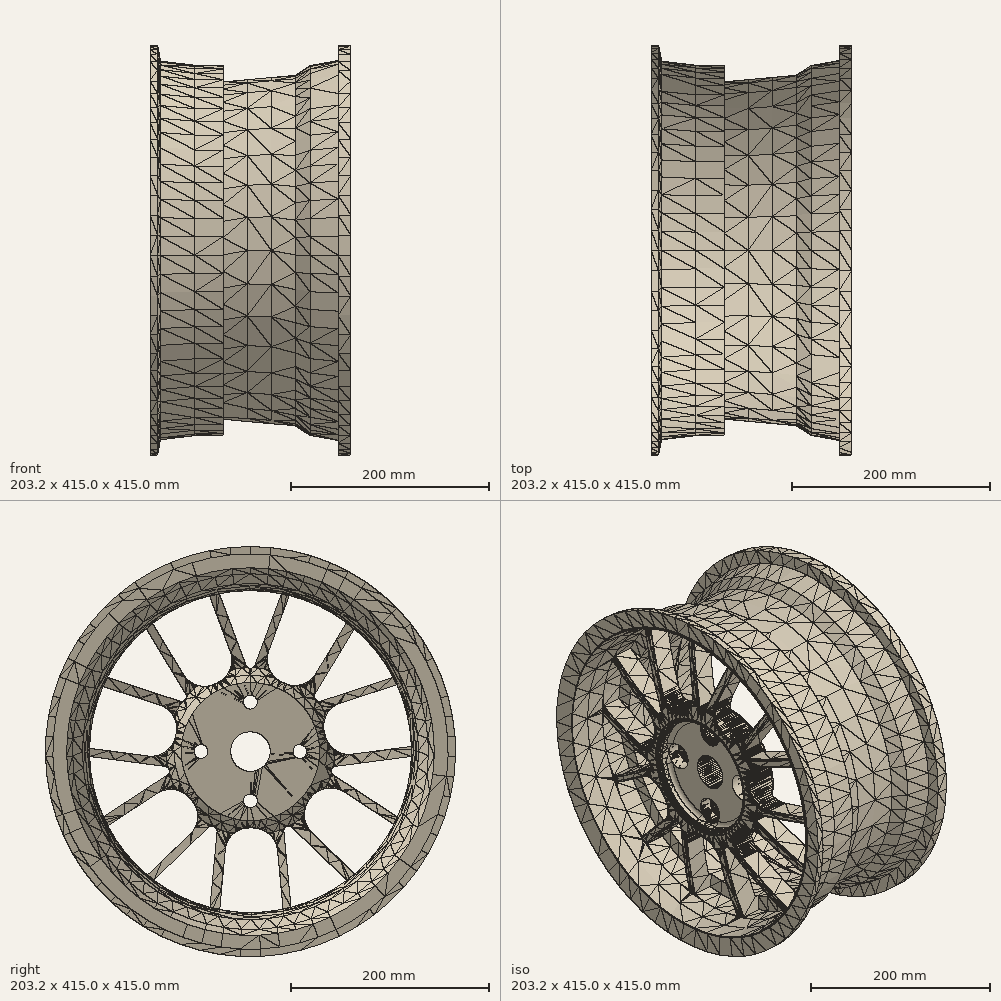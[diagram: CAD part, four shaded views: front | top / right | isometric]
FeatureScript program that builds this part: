
annotation { "Feature Type Name" : "Feature", "Feature Type Description" : "" }
export const myFeature = defineFeature(function(context is Context, id is Id, definition is map)
    precondition{}
    {
        {
            var Q0;
            Q0=qCreatedBy(makeId("Front.planeOp"),FACE);
            var sketch = newSketch(context, id + "F0", { "sketchPlane" : qUnion([Q0])});
            skLineSegment(sketch, "E0", {"start": v(0, 0) * mm, "end": v(203.2, 0) * mm});
            skLineSegment(sketch, "E1", {"start": v(203.2, 0) * mm, "end": v(203.2, 207.5) * mm});
            skPoint(sketch, "E2", {"position": v(203.2, 200) * mm});
            skLineSegment(sketch, "E3", {"start": v(203.2, 200) * mm, "end": v(197.7, 200) * mm});
            skPoint(sketch, "E4", {"position": v(197.7, 186) * mm});
            skLineSegment(sketch, "E5", {"start": v(197.7, 200) * mm, "end": v(197.7, 186) * mm});
            skPoint(sketch, "E6", {"position": v(164.7, 180) * mm});
            skLineSegment(sketch, "E7", {"start": v(164.7, 180) * mm, "end": v(197.7, 186) * mm});
            skPoint(sketch, "E8", {"position": v(149.7, 170) * mm});
            skLineSegment(sketch, "E9", {"start": v(164.7, 180) * mm, "end": v(149.7, 170) * mm});
            skPoint(sketch, "E10", {"position": v(66.7, 162.5) * mm});
            skLineSegment(sketch, "E11", {"start": v(66.7, 162.5) * mm, "end": v(149.7, 170) * mm});
            skLineSegment(sketch, "E12", {"start": v(203.2, 207.5) * mm, "end": v(66.7, 207.5) * mm});
            skLineSegment(sketch, "E13", {"start": v(0, 0) * mm, "end": v(0, 207.5) * mm});
            skPoint(sketch, "E14", {"position": v(2.5, 185) * mm});
            skPoint(sketch, "E15", {"position": v(45, 180) * mm});
            skLineSegment(sketch, "E16", {"start": v(45, 180) * mm, "end": v(66.7, 162.5) * mm});
            skLineSegment(sketch, "E17", {"start": v(2.5, 185) * mm, "end": v(45, 180) * mm});
            skLineSegment(sketch, "E18", {"start": v(0, 207.5) * mm, "end": v(66.7, 207.5) * mm});
            skLineSegment(sketch, "E19", {"start": v(2.5, 185) * mm, "end": v(0, 185) * mm});
            skLineSegment(sketch, "E20", {"start": v(2.5, 185) * mm, "end": v(2.5, 185.9) * mm});
            skLineSegment(sketch, "E21", {"start": v(3.1, 186.5) * mm, "end": v(3.4, 186.5) * mm});
            skLineSegment(sketch, "E22", {"start": v(0, 207.5) * mm, "end": v(4, 186.5) * mm});
            skPoint(sketch, "E23.visualSharp", {"position": v(2.5, 186.5) * mm});
            skArc(sketch, "E23.filletArc", {"start": v(3.1, 186.5) * mm, "mid": v(2.68, 186.32) * mm, "end": v(2.5, 185.9) * mm});
            skLineSegment(sketch, "E24", {"start": v(4, 185.9) * mm, "end": v(4, 185.5) * mm, "construction": true});
            skPoint(sketch, "E25.visualSharp", {"position": v(4, 186.5) * mm});
            skArc(sketch, "E25.filletArc", {"start": v(4, 185.9) * mm, "mid": v(3.82, 186.32) * mm, "end": v(3.4, 186.5) * mm});
            skLineSegment(sketch, "E26", {"start": v(4, 186.5) * mm, "end": v(4, 185.9) * mm});
            skLineSegment(sketch, "E27", {"start": v(66.7, 180) * mm, "end": v(45, 180) * mm});
            skLineSegment(sketch, "E28", {"start": v(66.7, 162.5) * mm, "end": v(66.7, 180) * mm});
            skArc(sketch, "E29", {"start": v(66.7, 162.5) * mm, "mid": v(58.94, 175.08) * mm, "end": v(45, 180) * mm});
            skLineSegment(sketch, "E30.0", {"start": v(203.2, 207.5) * mm, "end": v(190.2, 207.5) * mm});
            skLineSegment(sketch, "E30.1", {"start": v(66.03, 169.97) * mm, "end": v(66.7, 170.03) * mm});
            skLineSegment(sketch, "E30.2", {"start": v(161.83, 187.1) * mm, "end": v(147.13, 177.3) * mm});
            skLineSegment(sketch, "E30.3", {"start": v(161.83, 187.1) * mm, "end": v(190.2, 192.26) * mm});
            skLineSegment(sketch, "E30.4", {"start": v(190.2, 207.5) * mm, "end": v(190.2, 192.26) * mm});
            skLineSegment(sketch, "E31.0", {"start": v(10.67, 191.6) * mm, "end": v(45.44, 187.5) * mm});
            skLineSegment(sketch, "E31.1", {"start": v(7.63, 207.5) * mm, "end": v(10.67, 191.6) * mm});
            skLineSegment(sketch, "E32.0", {"start": v(74.2, 187.5) * mm, "end": v(45.44, 187.5) * mm});
            skLineSegment(sketch, "E32.1", {"start": v(74.2, 162.5) * mm, "end": v(74.2, 163.18) * mm});
            skLineSegment(sketch, "E33.trimOffspring", {"start": v(74.2, 170.7) * mm, "end": v(74.2, 187.5) * mm});
            skLineSegment(sketch, "E34.trimOffspring", {"start": v(74.2, 170.7) * mm, "end": v(147.13, 177.3) * mm});
            skPoint(sketch, "E35", {"position": v(45, -180) * mm});
            skPoint(sketch, "E36", {"position": v(16, 0) * mm});
            skArc(sketch, "E37", {"start": v(45, 180) * mm, "mid": v(23.3, 91.16) * mm, "end": v(16, 0) * mm});
            skArc(sketch, "E38.0", {"start": v(66.7, 162.54) * mm, "mid": v(48.21, 82.2) * mm, "end": v(42, 0) * mm});
            skLineSegment(sketch, "E39", {"start": v(16, 0) * mm, "end": v(42, 0) * mm});
            skLineSegment(sketch, "E40", {"start": v(16, 0) * mm, "end": v(16, 20) * mm});
            skLineSegment(sketch, "E41", {"start": v(16, 20) * mm, "end": v(76, 20) * mm});
            skPoint(sketch, "E42", {"position": v(66.2, 70) * mm});
            skPoint(sketch, "E43", {"position": v(48.64, 85) * mm});
            skLineSegment(sketch, "E44", {"start": v(66.2, 70) * mm, "end": v(48.64, 85) * mm});
            skLineSegment(sketch, "E45", {"start": v(66.2, 70) * mm, "end": v(66.2, 0) * mm});
            skSolve(sketch);
        }
        {
            var Q0;
            {var subQ3=sQuery(id+"F0.wireOp",EDGE,"E38.0");var subQ5=sQuery(id+"F0.wireOp",EDGE,"E41");var subQ7=makeQuery(id+"F0.imprint","INTERSECT",VERTEX,{"derivedFrom":[subQ3,subQ5]});Q0=makeQuery(id+"F0.imprint","IMPRINT",FACE,{"disambiguationData":[TD([[makeQuery(id+"F0.imprint","IMPRINT",EDGE,{"disambiguationData":[TD([[subQ7,1.0]])],"derivedFrom":subQ3}),-1.0]])]});}
            var Q1;
            {var subQ1=sQuery(id+"F0.wireOp",EDGE,"E16");var subQ3=sQuery(id+"F0.wireOp",EDGE,"E38.0");var subQ4=makeQuery(id+"F0.imprint","INTERSECT",VERTEX,{"derivedFrom":[subQ1,subQ3]});Q1=makeQuery(id+"F0.imprint","IMPRINT",FACE,{"disambiguationData":[TD([[makeQuery(id+"F0.imprint","IMPRINT",EDGE,{"disambiguationData":[TD([[subQ4,1.0]])],"derivedFrom":subQ3}),-1.0]])]});}
            var Q2;
            {var subQ1=sQuery(id+"F0.wireOp",EDGE,"E27");Q2=makeQuery(id+"F0.imprint","IMPRINT",FACE,{"disambiguationData":[TD([[makeQuery(id+"F0.imprint","IMPRINT",EDGE,{"derivedFrom":subQ1}),1.0]])]});}
            var Q3;
            {var subQ7=sQuery(id+"F0.wireOp",EDGE,"E3");Q3=makeQuery(id+"F0.imprint","IMPRINT",FACE,{"disambiguationData":[TD([[makeQuery(id+"F0.imprint","IMPRINT",EDGE,{"derivedFrom":subQ7}),-1.0]])]});}
            var Q4;
            {var subQ0=sQuery(id+"F0.wireOp",EDGE,"E44");Q4=makeQuery(id+"F0.imprint","IMPRINT",FACE,{"disambiguationData":[TD([[makeQuery(id+"F0.imprint","IMPRINT",EDGE,{"derivedFrom":subQ0}),1.0]])]});}
            var Q5;
            Q5=sQuery(id+"F0.wireOp",EDGE,"E0");
            revolve(context, id + "F1", {"entities" : qUnion([Q0, Q1, Q2, Q3, Q4]), "axis" : qUnion([Q5]), "revolveType" : RevolveType.FULL});
        }
        {
            var Q0;
            Q0=qCreatedBy(makeId("Right.planeOp"),FACE);
            cPlane(context, id + "F2", {"entities" : qUnion([Q0]), "cplaneType" : CPlaneType.OFFSET, "offset" : 16 * mm, "width" : 150 * mm, "height" : 150 * mm});
        }
        {
            var Q0;
            Q0=qCreatedBy(id+"F2.planeOp",FACE);
            var sketch = newSketch(context, id + "F3", { "sketchPlane" : qUnion([Q0])});
            skCircle(sketch, "E46.0", {"center": v(0, 0) * mm, "radius": 20 * mm});
            skCircle(sketch, "E47", {"center": v(0, 0) * mm, "radius": 50 * mm, "construction": true});
            skPoint(sketch, "E48", {"position": v(0, 50) * mm});
            skPoint(sketch, "E49", {"position": v(50, 0) * mm});
            skPoint(sketch, "E50", {"position": v(0, -50) * mm});
            skPoint(sketch, "E51", {"position": v(-50, 0) * mm});
            skCircle(sketch, "E52", {"center": v(0, 50) * mm, "radius": 7 * mm});
            skCircle(sketch, "E53", {"center": v(-50, 0) * mm, "radius": 7 * mm});
            skCircle(sketch, "E54", {"center": v(0, -50) * mm, "radius": 7 * mm});
            skCircle(sketch, "E55", {"center": v(50, 0) * mm, "radius": 7 * mm});
            skCircle(sketch, "E56", {"center": v(0, 0) * mm, "radius": 75 * mm});
            skPoint(sketch, "E57", {"position": v(0, 75) * mm});
            skCircle(sketch, "E58.0", {"center": v(0, 0) * mm, "radius": 180 * mm});
            skLineSegment(sketch, "E59", {"start": v(0, 75) * mm, "end": v(0, 180) * mm});
            skPoint(sketch, "E60.orphan", {"position": v(0, 193.6) * mm});
            skPoint(sketch, "E61", {"position": v(-37.5, 180) * mm});
            skLineSegment(sketch, "E62", {"start": v(-37.5, 180) * mm, "end": v(37.5, 180) * mm});
            skLineSegment(sketch, "E63", {"start": v(37.5, 180) * mm, "end": v(37.5, 176.05) * mm});
            skLineSegment(sketch, "E64", {"start": v(-37.5, 180) * mm, "end": v(-37.5, 176.05) * mm});
            skLineSegment(sketch, "E65", {"start": v(-37.5, 176.05) * mm, "end": v(-4.69, 87.63) * mm});
            skLineSegment(sketch, "E66", {"start": v(4.69, 87.63) * mm, "end": v(37.5, 176.05) * mm});
            skArc(sketch, "E67.filletArc", {"start": v(-4.69, 87.63) * mm, "mid": v(0, 84.37) * mm, "end": v(4.69, 87.63) * mm});
            skLineSegment(sketch, "E68.1.0", {"start": v(-65.6, 58.3) * mm, "end": v(-114.26, 139.08) * mm});
            skLineSegment(sketch, "E68.1.1", {"start": v(-161.02, 80.45) * mm, "end": v(-71.44, 50.97) * mm});
            skArc(sketch, "E68.1.2", {"start": v(-71.44, 50.97) * mm, "mid": v(-65.96, 52.6) * mm, "end": v(-65.6, 58.3) * mm});
            skLineSegment(sketch, "E68.2.0", {"start": v(-86.48, -14.93) * mm, "end": v(-179.98, -2.62) * mm});
            skLineSegment(sketch, "E68.2.1", {"start": v(-163.3, -75.73) * mm, "end": v(-84.4, -24.07) * mm});
            skArc(sketch, "E68.2.2", {"start": v(-84.4, -24.07) * mm, "mid": v(-82.26, -18.77) * mm, "end": v(-86.48, -14.93) * mm});
            skLineSegment(sketch, "E68.3.0", {"start": v(-42.25, -76.92) * mm, "end": v(-110.17, -142.35) * mm});
            skLineSegment(sketch, "E68.3.1", {"start": v(-42.6, -174.89) * mm, "end": v(-33.8, -80.99) * mm});
            skArc(sketch, "E68.3.2", {"start": v(-33.8, -80.99) * mm, "mid": v(-36.6, -76.02) * mm, "end": v(-42.25, -76.92) * mm});
            skLineSegment(sketch, "E68.4.0", {"start": v(33.8, -80.99) * mm, "end": v(42.6, -174.89) * mm});
            skLineSegment(sketch, "E68.4.1", {"start": v(110.17, -142.35) * mm, "end": v(42.25, -76.92) * mm});
            skArc(sketch, "E68.4.2", {"start": v(42.25, -76.92) * mm, "mid": v(36.6, -76.02) * mm, "end": v(33.8, -80.99) * mm});
            skLineSegment(sketch, "E68.5.0", {"start": v(84.4, -24.07) * mm, "end": v(163.3, -75.73) * mm});
            skLineSegment(sketch, "E68.5.1", {"start": v(179.98, -2.62) * mm, "end": v(86.48, -14.93) * mm});
            skArc(sketch, "E68.5.2", {"start": v(86.48, -14.93) * mm, "mid": v(82.26, -18.77) * mm, "end": v(84.4, -24.07) * mm});
            skLineSegment(sketch, "E68.6.0", {"start": v(71.44, 50.97) * mm, "end": v(161.02, 80.45) * mm});
            skLineSegment(sketch, "E68.6.1", {"start": v(114.26, 139.08) * mm, "end": v(65.6, 58.3) * mm});
            skArc(sketch, "E68.6.2", {"start": v(65.6, 58.3) * mm, "mid": v(65.96, 52.6) * mm, "end": v(71.44, 50.97) * mm});
            skPoint(sketch, "E69", {"position": v(45.5, 174.15) * mm});
            skLineSegment(sketch, "E70", {"start": v(45.5, 174.15) * mm, "end": v(18.69, 101.9) * mm});
            skPoint(sketch, "E71", {"position": v(106.26, 145.29) * mm});
            skLineSegment(sketch, "E72", {"start": v(106.26, 145.29) * mm, "end": v(66.32, 79) * mm});
            skLineSegment(sketch, "E73", {"start": v(34.22, 69.29) * mm, "end": v(31.44, 70.6) * mm});
            skPoint(sketch, "E74.visualSharp", {"position": v(10.7, 80.4) * mm});
            skArc(sketch, "E74.filletArc", {"start": v(18.69, 101.9) * mm, "mid": v(18.97, 83.77) * mm, "end": v(31.44, 70.6) * mm});
            skPoint(sketch, "E75.visualSharp", {"position": v(54.65, 59.63) * mm});
            skArc(sketch, "E75.filletArc", {"start": v(34.22, 69.29) * mm, "mid": v(52.14, 67.96) * mm, "end": v(66.32, 79) * mm});
            skLineSegment(sketch, "E76.1.0", {"start": v(-47.34, 173.66) * mm, "end": v(-20.4, 101.1) * mm});
            skLineSegment(sketch, "E76.1.1", {"start": v(-107.8, 144.16) * mm, "end": v(-68.02, 78.15) * mm});
            skArc(sketch, "E76.1.2", {"start": v(-68.02, 78.15) * mm, "mid": v(-53.66, 67.06) * mm, "end": v(-35.6, 68.6) * mm});
            skArc(sketch, "E76.1.3", {"start": v(-32.84, 69.96) * mm, "mid": v(-20.63, 83.14) * mm, "end": v(-20.4, 101.1) * mm});
            skLineSegment(sketch, "E76.1.4", {"start": v(-32.84, 69.96) * mm, "end": v(-35.6, 68.6) * mm});
            skLineSegment(sketch, "E76.2.0", {"start": v(-165.3, 71.27) * mm, "end": v(-91.77, 47.08) * mm});
            skLineSegment(sketch, "E76.2.1", {"start": v(-179.91, 5.6) * mm, "end": v(-103.5, -4.46) * mm});
            skArc(sketch, "E76.2.2", {"start": v(-103.5, -4.46) * mm, "mid": v(-85.9, -0.14) * mm, "end": v(-75.83, 14.94) * mm});
            skArc(sketch, "E76.2.3", {"start": v(-75.17, 17.95) * mm, "mid": v(-77.86, 35.7) * mm, "end": v(-91.77, 47.08) * mm});
            skLineSegment(sketch, "E76.2.4", {"start": v(-75.17, 17.95) * mm, "end": v(-75.83, 14.94) * mm});
            skLineSegment(sketch, "E76.3.0", {"start": v(-158.78, -84.8) * mm, "end": v(-94.02, -42.4) * mm});
            skLineSegment(sketch, "E76.3.1", {"start": v(-116.56, -137.17) * mm, "end": v(-61.05, -83.7) * mm});
            skArc(sketch, "E76.3.2", {"start": v(-61.05, -83.7) * mm, "mid": v(-53.44, -67.24) * mm, "end": v(-58.96, -49.97) * mm});
            skArc(sketch, "E76.3.3", {"start": v(-60.9, -47.58) * mm, "mid": v(-76.46, -38.61) * mm, "end": v(-94.02, -42.4) * mm});
            skLineSegment(sketch, "E76.3.4", {"start": v(-60.9, -47.58) * mm, "end": v(-58.96, -49.97) * mm});
            skLineSegment(sketch, "E76.4.0", {"start": v(-32.7, -177) * mm, "end": v(-25.48, -99.94) * mm});
            skLineSegment(sketch, "E76.4.1", {"start": v(34.57, -176.65) * mm, "end": v(27.38, -99.92) * mm});
            skArc(sketch, "E76.4.2", {"start": v(27.38, -99.92) * mm, "mid": v(19.25, -83.7) * mm, "end": v(2.3, -77.25) * mm});
            skArc(sketch, "E76.4.3", {"start": v(-0.77, -77.28) * mm, "mid": v(-17.49, -83.85) * mm, "end": v(-25.48, -99.94) * mm});
            skLineSegment(sketch, "E76.4.4", {"start": v(-0.77, -77.28) * mm, "end": v(2.3, -77.25) * mm});
            skLineSegment(sketch, "E76.5.0", {"start": v(118, -135.93) * mm, "end": v(62.25, -82.23) * mm});
            skLineSegment(sketch, "E76.5.1", {"start": v(159.66, -83.11) * mm, "end": v(95.2, -40.9) * mm});
            skArc(sketch, "E76.5.2", {"start": v(95.2, -40.9) * mm, "mid": v(77.45, -37.14) * mm, "end": v(61.84, -46.37) * mm});
            skArc(sketch, "E76.5.3", {"start": v(59.94, -48.78) * mm, "mid": v(54.66, -65.95) * mm, "end": v(62.25, -82.23) * mm});
            skLineSegment(sketch, "E76.5.4", {"start": v(59.94, -48.78) * mm, "end": v(61.84, -46.37) * mm});
            skLineSegment(sketch, "E76.6.0", {"start": v(179.84, 7.5) * mm, "end": v(103.1, -2.6) * mm});
            skLineSegment(sketch, "E76.6.1", {"start": v(164.53, 73.01) * mm, "end": v(91.32, 48.93) * mm});
            skArc(sketch, "E76.6.2", {"start": v(91.32, 48.93) * mm, "mid": v(77.32, 37.4) * mm, "end": v(74.8, 19.44) * mm});
            skArc(sketch, "E76.6.3", {"start": v(75.5, 16.45) * mm, "mid": v(85.64, 1.61) * mm, "end": v(103.1, -2.6) * mm});
            skLineSegment(sketch, "E76.6.4", {"start": v(75.5, 16.45) * mm, "end": v(74.8, 19.44) * mm});
            skSolve(sketch);
        }
        {
            var Q0;
            {var subQ0=sQuery(id+"F3.wireOp",EDGE,"E68.6.0");Q0=makeQuery(id+"F3.imprint","IMPRINT",FACE,{"disambiguationData":[TD([[makeQuery(id+"F3.imprint","IMPRINT",EDGE,{"derivedFrom":subQ0}),1.0]])]});}
            var Q1;
            {var subQ3=sQuery(id+"F3.wireOp",EDGE,"E66");Q1=makeQuery(id+"F3.imprint","IMPRINT",FACE,{"disambiguationData":[TD([[makeQuery(id+"F3.imprint","IMPRINT",EDGE,{"derivedFrom":subQ3}),1.0]])]});}
            var Q2;
            {var subQ3=sQuery(id+"F3.wireOp",EDGE,"E65");Q2=makeQuery(id+"F3.imprint","IMPRINT",FACE,{"disambiguationData":[TD([[makeQuery(id+"F3.imprint","IMPRINT",EDGE,{"derivedFrom":subQ3}),1.0]])]});}
            var Q3;
            {var subQ0=sQuery(id+"F3.wireOp",EDGE,"E68.1.0");Q3=makeQuery(id+"F3.imprint","IMPRINT",FACE,{"disambiguationData":[TD([[makeQuery(id+"F3.imprint","IMPRINT",EDGE,{"derivedFrom":subQ0}),1.0]])]});}
            var Q4;
            {var subQ0=sQuery(id+"F3.wireOp",EDGE,"E68.2.0");Q4=makeQuery(id+"F3.imprint","IMPRINT",FACE,{"disambiguationData":[TD([[makeQuery(id+"F3.imprint","IMPRINT",EDGE,{"derivedFrom":subQ0}),1.0]])]});}
            var Q5;
            {var subQ0=sQuery(id+"F3.wireOp",EDGE,"E68.3.0");Q5=makeQuery(id+"F3.imprint","IMPRINT",FACE,{"disambiguationData":[TD([[makeQuery(id+"F3.imprint","IMPRINT",EDGE,{"derivedFrom":subQ0}),1.0]])]});}
            var Q6;
            {var subQ0=sQuery(id+"F3.wireOp",EDGE,"E68.4.0");Q6=makeQuery(id+"F3.imprint","IMPRINT",FACE,{"disambiguationData":[TD([[makeQuery(id+"F3.imprint","IMPRINT",EDGE,{"derivedFrom":subQ0}),1.0]])]});}
            var Q7;
            {var subQ0=sQuery(id+"F3.wireOp",EDGE,"E68.5.0");Q7=makeQuery(id+"F3.imprint","IMPRINT",FACE,{"disambiguationData":[TD([[makeQuery(id+"F3.imprint","IMPRINT",EDGE,{"derivedFrom":subQ0}),1.0]])]});}
            var Q8;
            Q8=makeQuery(id+"F3.imprint","IMPRINT",FACE,{"disambiguationData":[TD([[makeQuery(id+"F3.imprint","IMPRINT",EDGE,{"derivedFrom":sQuery(id+"F3.wireOp",EDGE,"E52")}),1.0]])]});
            var Q9;
            Q9=makeQuery(id+"F3.imprint","IMPRINT",FACE,{"disambiguationData":[TD([[makeQuery(id+"F3.imprint","IMPRINT",EDGE,{"derivedFrom":sQuery(id+"F3.wireOp",EDGE,"E55")}),1.0]])]});
            var Q10;
            Q10=makeQuery(id+"F3.imprint","IMPRINT",FACE,{"disambiguationData":[TD([[makeQuery(id+"F3.imprint","IMPRINT",EDGE,{"derivedFrom":sQuery(id+"F3.wireOp",EDGE,"E54")}),1.0]])]});
            var Q11;
            Q11=makeQuery(id+"F3.imprint","IMPRINT",FACE,{"disambiguationData":[TD([[makeQuery(id+"F3.imprint","IMPRINT",EDGE,{"derivedFrom":sQuery(id+"F3.wireOp",EDGE,"E53")}),1.0]])]});
            var Q12;
            {var subQ1=sQuery(id+"F3.wireOp",EDGE,"E76.5.0");Q12=makeQuery(id+"F3.imprint","IMPRINT",FACE,{"disambiguationData":[TD([[makeQuery(id+"F3.imprint","IMPRINT",EDGE,{"derivedFrom":subQ1}),-1.0]])]});}
            var Q13;
            {var subQ1=sQuery(id+"F3.wireOp",EDGE,"E76.6.0");Q13=makeQuery(id+"F3.imprint","IMPRINT",FACE,{"disambiguationData":[TD([[makeQuery(id+"F3.imprint","IMPRINT",EDGE,{"derivedFrom":subQ1}),-1.0]])]});}
            var Q14;
            {var subQ1=sQuery(id+"F3.wireOp",EDGE,"E76.4.0");Q14=makeQuery(id+"F3.imprint","IMPRINT",FACE,{"disambiguationData":[TD([[makeQuery(id+"F3.imprint","IMPRINT",EDGE,{"derivedFrom":subQ1}),-1.0]])]});}
            var Q15;
            {var subQ1=sQuery(id+"F3.wireOp",EDGE,"E76.3.0");Q15=makeQuery(id+"F3.imprint","IMPRINT",FACE,{"disambiguationData":[TD([[makeQuery(id+"F3.imprint","IMPRINT",EDGE,{"derivedFrom":subQ1}),-1.0]])]});}
            var Q16;
            {var subQ0=sQuery(id+"F3.wireOp",EDGE,"E76.2.0");Q16=makeQuery(id+"F3.imprint","IMPRINT",FACE,{"disambiguationData":[TD([[makeQuery(id+"F3.imprint","IMPRINT",EDGE,{"derivedFrom":subQ0}),-1.0]])]});}
            var Q17;
            {var subQ1=sQuery(id+"F3.wireOp",EDGE,"E76.1.0");Q17=makeQuery(id+"F3.imprint","IMPRINT",FACE,{"disambiguationData":[TD([[makeQuery(id+"F3.imprint","IMPRINT",EDGE,{"derivedFrom":subQ1}),-1.0]])]});}
            var Q18;
            {var subQ1=sQuery(id+"F3.wireOp",EDGE,"E70");Q18=makeQuery(id+"F3.imprint","IMPRINT",FACE,{"disambiguationData":[TD([[makeQuery(id+"F3.imprint","IMPRINT",EDGE,{"derivedFrom":subQ1}),1.0]])]});}
            extrude(context, id + "F4", {"entities" : qUnion([Q0, Q1, Q2, Q3, Q4, Q5, Q6, Q7, Q8, Q9, Q10, Q11, Q12, Q13, Q14, Q15, Q16, Q17, Q18]), "operationType" : NewBodyOperationType.REMOVE, "depth" : 55 * mm});
        }
        {
            var Q0;
            Q0=qCreatedBy(id+"F2.planeOp",FACE);
            var sketch = newSketch(context, id + "F5", { "sketchPlane" : qUnion([Q0])});
            skCircle(sketch, "E77.0", {"center": v(0, 0) * mm, "radius": 20 * mm});
            skCircle(sketch, "E78", {"center": v(0, 0) * mm, "radius": 65 * mm});
            skCircle(sketch, "E79.0", {"center": v(0, 50) * mm, "radius": 7 * mm, "construction": true});
            skCircle(sketch, "E80.0", {"center": v(50, 0) * mm, "radius": 7 * mm, "construction": true});
            skCircle(sketch, "E81.0", {"center": v(-50, 0) * mm, "radius": 7 * mm, "construction": true});
            skCircle(sketch, "E82.0", {"center": v(0, -50) * mm, "radius": 7 * mm, "construction": true});
            skCircle(sketch, "E83", {"center": v(0, 50) * mm, "radius": 15 * mm});
            skCircle(sketch, "E84", {"center": v(-50, 0) * mm, "radius": 15 * mm});
            skCircle(sketch, "E85", {"center": v(0, -50) * mm, "radius": 15 * mm});
            skCircle(sketch, "E86", {"center": v(50, 0) * mm, "radius": 15 * mm});
            skSolve(sketch);
        }
        {
            var Q0;
            Q0 = qSketchRegion(id + "F5", true);
            var Q1;
            {var subQ0=sQuery(id+"F5.wireOp",EDGE,"E83");var subQ1=sQuery(id+"F5.wireOp",EDGE,"E77.0");var subQ2=makeQuery(id+"F5.imprint","INTERSECT",VERTEX,{"disambiguationData":[OD(0.0)],"derivedFrom":[subQ1,subQ0]});Q1=makeQuery(id+"F5.imprint","IMPRINT",FACE,{"disambiguationData":[TD([[makeQuery(id+"F5.imprint","IMPRINT",EDGE,{"disambiguationData":[TD([[subQ2,-1.0]])],"derivedFrom":subQ1}),-1.0]])]});}
            var Q2;
            {var subQ0=sQuery(id+"F5.wireOp",EDGE,"E85");var subQ1=sQuery(id+"F5.wireOp",EDGE,"E77.0");var subQ2=makeQuery(id+"F5.imprint","INTERSECT",VERTEX,{"disambiguationData":[OD(0.0)],"derivedFrom":[subQ1,subQ0]});Q2=makeQuery(id+"F5.imprint","IMPRINT",FACE,{"disambiguationData":[TD([[makeQuery(id+"F5.imprint","IMPRINT",EDGE,{"disambiguationData":[TD([[subQ2,-1.0]])],"derivedFrom":subQ1}),-1.0]])]});}
            var Q3;
            {var subQ0=sQuery(id+"F5.wireOp",EDGE,"E84");var subQ1=sQuery(id+"F5.wireOp",EDGE,"E77.0");var subQ2=makeQuery(id+"F5.imprint","INTERSECT",VERTEX,{"disambiguationData":[OD(0.0)],"derivedFrom":[subQ1,subQ0]});Q3=makeQuery(id+"F5.imprint","IMPRINT",FACE,{"disambiguationData":[TD([[makeQuery(id+"F5.imprint","IMPRINT",EDGE,{"disambiguationData":[TD([[subQ2,-1.0]])],"derivedFrom":subQ1}),-1.0]])]});}
            var Q4;
            {var subQ0=sQuery(id+"F5.wireOp",EDGE,"E86");var subQ1=sQuery(id+"F5.wireOp",EDGE,"E77.0");var subQ2=makeQuery(id+"F5.imprint","INTERSECT",VERTEX,{"disambiguationData":[OD(0.0)],"derivedFrom":[subQ1,subQ0]});Q4=makeQuery(id+"F5.imprint","IMPRINT",FACE,{"disambiguationData":[TD([[makeQuery(id+"F5.imprint","IMPRINT",EDGE,{"disambiguationData":[TD([[subQ2,1.0]])],"derivedFrom":subQ1}),-1.0]])]});}
            var Q5;
            Q5=makeQuery(id+"F5.imprint","IMPRINT",FACE,{"disambiguationData":[TD([[makeQuery(id+"F5.imprint","IMPRINT",EDGE,{"derivedFrom":sQuery(id+"F5.wireOp",EDGE,"E86")}),1.0]])]});
            var Q6;
            Q6=makeQuery(id+"F5.imprint","IMPRINT",FACE,{"disambiguationData":[TD([[makeQuery(id+"F5.imprint","IMPRINT",EDGE,{"derivedFrom":sQuery(id+"F5.wireOp",EDGE,"E83")}),1.0]])]});
            var Q7;
            Q7=makeQuery(id+"F5.imprint","IMPRINT",FACE,{"disambiguationData":[TD([[makeQuery(id+"F5.imprint","IMPRINT",EDGE,{"derivedFrom":sQuery(id+"F5.wireOp",EDGE,"E84")}),1.0]])]});
            var Q8;
            Q8=makeQuery(id+"F5.imprint","IMPRINT",FACE,{"disambiguationData":[TD([[makeQuery(id+"F5.imprint","IMPRINT",EDGE,{"derivedFrom":sQuery(id+"F5.wireOp",EDGE,"E85")}),1.0]])]});
            extrude(context, id + "F6", {"entities" : qUnion([Q0, Q1, Q2, Q3, Q4, Q5, Q6, Q7, Q8]), "operationType" : NewBodyOperationType.REMOVE, "depth" : 20 * mm});
        }
        {
            var Q0;
            Q0=makeQuery(id+"F6.boolean.opBoolean","COPY",FACE,{"derivedFrom":makeQuery(id+"F6.opExtrude","CAP_FACE",FACE,{"disambiguationData":[OSD([sQuery(id+"F5.wireOp",EDGE,"E77.0"),sQuery(id+"F5.wireOp",EDGE,"E78")])],"isStart":false})});
            var sketch = newSketch(context, id + "F7", { "sketchPlane" : qUnion([Q0])});
            skCircle(sketch, "E87.0", {"center": v(0, 50) * mm, "radius": 7 * mm, "construction": true});
            skCircle(sketch, "E88", {"center": v(0, 50) * mm, "radius": 15 * mm});
            skCircle(sketch, "E89.1.0", {"center": v(-50, 0) * mm, "radius": 15 * mm});
            skCircle(sketch, "E89.2.0", {"center": v(0, -50) * mm, "radius": 15 * mm});
            skCircle(sketch, "E89.3.0", {"center": v(50, 0) * mm, "radius": 15 * mm});
            skPoint(sketch, "E89.center", {"position": v(0, 0) * mm});
            skSolve(sketch);
        }
        {
            var Q0;
            Q0 = qSketchRegion(id + "F7", true);
            extrude(context, id + "F8", {"entities" : qUnion([Q0]), "operationType" : NewBodyOperationType.REMOVE, "oppositeDirection" : true, "depth" : 15 * mm});
        }
        {
            var Q0;
            Q0=makeQuery(id+"F6.boolean.opBoolean","INTERSECT",EDGE,{"derivedFrom":[makeQuery(id+"F1.opRevolve","SWEPT_FACE",FACE,{"disambiguationData":[OSD([sQuery(id+"F0.wireOp",EDGE,"E37")])]}),makeQuery(id+"F6.opExtrude","SWEPT_FACE",FACE,{"disambiguationData":[OSD([sQuery(id+"F5.wireOp",EDGE,"E78")])]})]});
            var Q1;
            {var subQ0=sQuery(id+"F5.wireOp",EDGE,"E78");Q1=makeQuery(id+"F8.boolean.opBoolean","SPLIT",EDGE,{"disambiguationData":[TD([makeQuery(id+"F6.boolean.opBoolean","COPY",FACE,{"derivedFrom":makeQuery(id+"F6.opExtrude","CAP_FACE",FACE,{"disambiguationData":[OSD([sQuery(id+"F5.wireOp",EDGE,"E77.0"),subQ0])],"isStart":false})}),makeQuery(id+"F6.boolean.opBoolean","COPY",FACE,{"derivedFrom":makeQuery(id+"F6.opExtrude","SWEPT_FACE",FACE,{"disambiguationData":[OSD([subQ0])]})}),makeQuery(id+"F8.opExtrude","SWEPT_FACE",FACE,{"disambiguationData":[OSD([sQuery(id+"F7.wireOp",EDGE,"E88")])]}),makeQuery(id+"F8.opExtrude","SWEPT_FACE",FACE,{"disambiguationData":[OSD([sQuery(id+"F7.wireOp",EDGE,"E89.1.0")])]})])],"derivedFrom":makeQuery(id+"F6.boolean.opBoolean","COPY",EDGE,{"derivedFrom":makeQuery(id+"F6.opExtrude","CAP_EDGE",EDGE,{"disambiguationData":[OSD([subQ0])],"isStart":false})})});}
            fillet(context, id + "F9", {"entities" : qUnion([Q0, Q1]), "radius" : 5 * mm, "tangentPropagation" : true, "allowEdgeOverflow" : false});
        }
        {
            var Q0;
            Q0=makeQuery(id+"F4.boolean.opBoolean","INTERSECT",EDGE,{"derivedFrom":[makeQuery(id+"F1.opRevolve","SWEPT_FACE",FACE,{"disambiguationData":[OSD([sQuery(id+"F0.wireOp",EDGE,"E37")])]}),makeQuery(id+"F4.opExtrude","SWEPT_FACE",FACE,{"disambiguationData":[OSD([sQuery(id+"F3.wireOp",EDGE,"E76.6.0")])]})]});
            var Q1;
            Q1=makeQuery(id+"F4.boolean.opBoolean","INTERSECT",EDGE,{"derivedFrom":[makeQuery(id+"F1.opRevolve","SWEPT_FACE",FACE,{"disambiguationData":[OSD([sQuery(id+"F0.wireOp",EDGE,"E37")])]}),makeQuery(id+"F4.opExtrude","SWEPT_FACE",FACE,{"disambiguationData":[OSD([sQuery(id+"F3.wireOp",EDGE,"E68.5.1")])]})]});
            var Q2;
            Q2=makeQuery(id+"F4.boolean.opBoolean","INTERSECT",EDGE,{"derivedFrom":[makeQuery(id+"F1.opRevolve","SWEPT_FACE",FACE,{"disambiguationData":[OSD([sQuery(id+"F0.wireOp",EDGE,"E37")])]}),makeQuery(id+"F4.opExtrude","SWEPT_FACE",FACE,{"disambiguationData":[OSD([sQuery(id+"F3.wireOp",EDGE,"E76.5.1")])]})]});
            var Q3;
            Q3=makeQuery(id+"F4.boolean.opBoolean","INTERSECT",EDGE,{"derivedFrom":[makeQuery(id+"F1.opRevolve","SWEPT_FACE",FACE,{"disambiguationData":[OSD([sQuery(id+"F0.wireOp",EDGE,"E37")])]}),makeQuery(id+"F4.opExtrude","SWEPT_FACE",FACE,{"disambiguationData":[OSD([sQuery(id+"F3.wireOp",EDGE,"E68.4.1")])]})]});
            var Q4;
            Q4=makeQuery(id+"F4.boolean.opBoolean","INTERSECT",EDGE,{"derivedFrom":[makeQuery(id+"F1.opRevolve","SWEPT_FACE",FACE,{"disambiguationData":[OSD([sQuery(id+"F0.wireOp",EDGE,"E37")])]}),makeQuery(id+"F4.opExtrude","SWEPT_FACE",FACE,{"disambiguationData":[OSD([sQuery(id+"F3.wireOp",EDGE,"E76.4.1")])]})]});
            var Q5;
            Q5=makeQuery(id+"F4.boolean.opBoolean","INTERSECT",EDGE,{"derivedFrom":[makeQuery(id+"F1.opRevolve","SWEPT_FACE",FACE,{"disambiguationData":[OSD([sQuery(id+"F0.wireOp",EDGE,"E37")])]}),makeQuery(id+"F4.opExtrude","SWEPT_FACE",FACE,{"disambiguationData":[OSD([sQuery(id+"F3.wireOp",EDGE,"E68.3.1")])]})]});
            var Q6;
            Q6=makeQuery(id+"F4.boolean.opBoolean","INTERSECT",EDGE,{"derivedFrom":[makeQuery(id+"F1.opRevolve","SWEPT_FACE",FACE,{"disambiguationData":[OSD([sQuery(id+"F0.wireOp",EDGE,"E37")])]}),makeQuery(id+"F4.opExtrude","SWEPT_FACE",FACE,{"disambiguationData":[OSD([sQuery(id+"F3.wireOp",EDGE,"E76.3.1")])]})]});
            var Q7;
            Q7=makeQuery(id+"F4.boolean.opBoolean","INTERSECT",EDGE,{"derivedFrom":[makeQuery(id+"F1.opRevolve","SWEPT_FACE",FACE,{"disambiguationData":[OSD([sQuery(id+"F0.wireOp",EDGE,"E37")])]}),makeQuery(id+"F4.opExtrude","SWEPT_FACE",FACE,{"disambiguationData":[OSD([sQuery(id+"F3.wireOp",EDGE,"E68.2.1")])]})]});
            var Q8;
            Q8=makeQuery(id+"F4.boolean.opBoolean","INTERSECT",EDGE,{"derivedFrom":[makeQuery(id+"F1.opRevolve","SWEPT_FACE",FACE,{"disambiguationData":[OSD([sQuery(id+"F0.wireOp",EDGE,"E37")])]}),makeQuery(id+"F4.opExtrude","SWEPT_FACE",FACE,{"disambiguationData":[OSD([sQuery(id+"F3.wireOp",EDGE,"E76.2.1")])]})]});
            var Q9;
            Q9=makeQuery(id+"F4.boolean.opBoolean","INTERSECT",EDGE,{"derivedFrom":[makeQuery(id+"F1.opRevolve","SWEPT_FACE",FACE,{"disambiguationData":[OSD([sQuery(id+"F0.wireOp",EDGE,"E37")])]}),makeQuery(id+"F4.opExtrude","SWEPT_FACE",FACE,{"disambiguationData":[OSD([sQuery(id+"F3.wireOp",EDGE,"E68.1.1")])]})]});
            var Q10;
            Q10=makeQuery(id+"F4.boolean.opBoolean","INTERSECT",EDGE,{"derivedFrom":[makeQuery(id+"F1.opRevolve","SWEPT_FACE",FACE,{"disambiguationData":[OSD([sQuery(id+"F0.wireOp",EDGE,"E37")])]}),makeQuery(id+"F4.opExtrude","SWEPT_FACE",FACE,{"disambiguationData":[OSD([sQuery(id+"F3.wireOp",EDGE,"E76.1.1")])]})]});
            var Q11;
            Q11=makeQuery(id+"F4.boolean.opBoolean","INTERSECT",EDGE,{"derivedFrom":[makeQuery(id+"F1.opRevolve","SWEPT_FACE",FACE,{"disambiguationData":[OSD([sQuery(id+"F0.wireOp",EDGE,"E37")])]}),makeQuery(id+"F4.opExtrude","SWEPT_FACE",FACE,{"disambiguationData":[OSD([sQuery(id+"F3.wireOp",EDGE,"E65")])]})]});
            var Q12;
            Q12=makeQuery(id+"F4.boolean.opBoolean","INTERSECT",EDGE,{"derivedFrom":[makeQuery(id+"F1.opRevolve","SWEPT_FACE",FACE,{"disambiguationData":[OSD([sQuery(id+"F0.wireOp",EDGE,"E37")])]}),makeQuery(id+"F4.opExtrude","SWEPT_FACE",FACE,{"disambiguationData":[OSD([sQuery(id+"F3.wireOp",EDGE,"E70")])]})]});
            var Q13;
            Q13=makeQuery(id+"F4.boolean.opBoolean","INTERSECT",EDGE,{"derivedFrom":[makeQuery(id+"F1.opRevolve","SWEPT_FACE",FACE,{"disambiguationData":[OSD([sQuery(id+"F0.wireOp",EDGE,"E37")])]}),makeQuery(id+"F4.opExtrude","SWEPT_FACE",FACE,{"disambiguationData":[OSD([sQuery(id+"F3.wireOp",EDGE,"E68.6.1")])]})]});
            fillet(context, id + "F10", {"entities" : qUnion([Q0, Q1, Q2, Q3, Q4, Q5, Q6, Q7, Q8, Q9, Q10, Q11, Q12, Q13]), "radius" : 2 * mm, "tangentPropagation" : true, "allowEdgeOverflow" : false});
        }
    });
